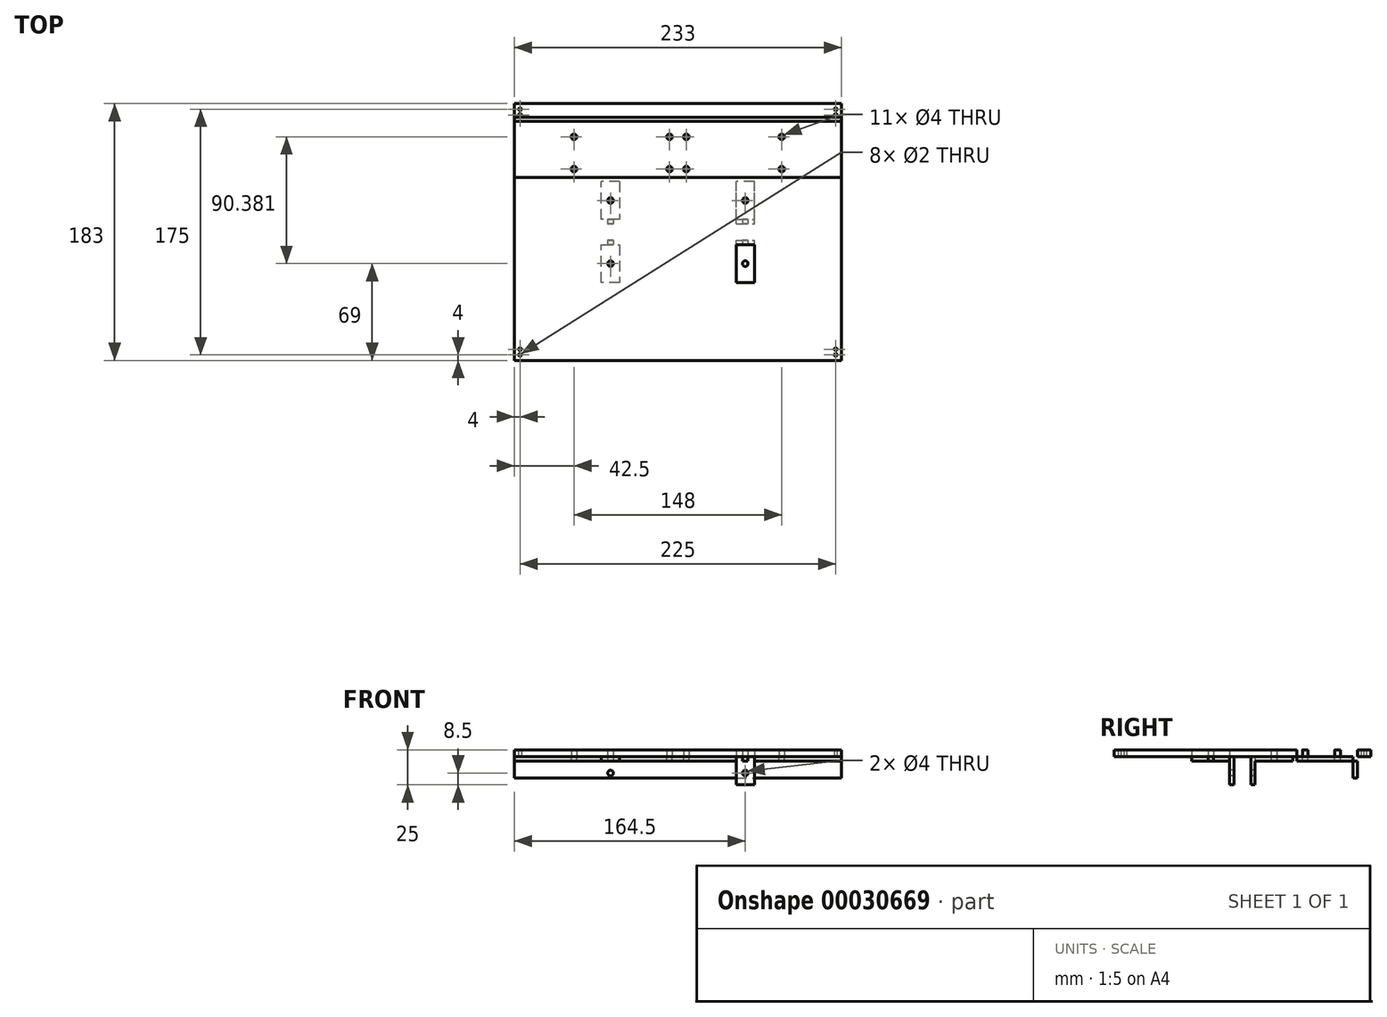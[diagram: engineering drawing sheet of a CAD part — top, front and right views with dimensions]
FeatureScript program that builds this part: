
annotation { "Feature Type Name" : "Feature", "Feature Type Description" : "" }
export const myFeature = defineFeature(function(context is Context, id is Id, definition is map)
    precondition{}
    {
        {
            var Q0;
            Q0=qCreatedBy(makeId("Top.planeOp"),FACE);
            var sketch = newSketch(context, id + "F0", { "sketchPlane" : qUnion([Q0])});
            skLineSegment(sketch, "E0.rect.bottom", {"start": v(116.5, 91.5) * mm, "end": v(-116.5, 91.5) * mm});
            skLineSegment(sketch, "E0.rect.top", {"start": v(116.5, -91.5) * mm, "end": v(-116.5, -91.5) * mm});
            skLineSegment(sketch, "E0.rect.left", {"start": v(116.5, 91.5) * mm, "end": v(116.5, -91.5) * mm});
            skLineSegment(sketch, "E0.rect.right", {"start": v(-116.5, 91.5) * mm, "end": v(-116.5, -91.5) * mm});
            skPoint(sketch, "E0.rect.middle", {"position": v(0, 0) * mm});
            skLineSegment(sketch, "E1", {"start": v(-116.5, -6) * mm, "end": v(116.5, -6) * mm});
            skLineSegment(sketch, "E2.MirrorCS", {"start": v(-116.5, 6) * mm, "end": v(116.5, 6) * mm});
            skLineSegment(sketch, "E3", {"start": v(-116.5, 9) * mm, "end": v(116.5, 9) * mm});
            skLineSegment(sketch, "E4", {"start": v(-116.5, -9) * mm, "end": v(116.5, -9) * mm});
            skLineSegment(sketch, "E5.bottom", {"start": v(-116.5, 6) * mm, "end": v(116.5, 6) * mm, "construction": true});
            skLineSegment(sketch, "E5.top", {"start": v(-116.5, 36) * mm, "end": v(116.5, 36) * mm, "construction": true});
            skLineSegment(sketch, "E5.left", {"start": v(-116.5, 6) * mm, "end": v(-116.5, 36) * mm});
            skLineSegment(sketch, "E5.right", {"start": v(116.5, 6) * mm, "end": v(116.5, 36) * mm});
            skLineSegment(sketch, "E6.bottom", {"start": v(-116.5, -6) * mm, "end": v(116.5, -6) * mm, "construction": true});
            skLineSegment(sketch, "E6.top", {"start": v(-116.5, -36) * mm, "end": v(116.5, -36) * mm, "construction": true});
            skLineSegment(sketch, "E6.left", {"start": v(-116.5, -6) * mm, "end": v(-116.5, -36) * mm});
            skLineSegment(sketch, "E6.right", {"start": v(116.5, -6) * mm, "end": v(116.5, -36) * mm});
            skCircle(sketch, "E7", {"center": v(-112.5, -87.5) * mm, "radius": 1 * mm});
            skCircle(sketch, "E8", {"center": v(-112.5, -83.5) * mm, "radius": 1 * mm});
            skLineSegment(sketch, "E9", {"start": v(-116.5, 0) * mm, "end": v(116.5, 0) * mm, "construction": true});
            skLineSegment(sketch, "E10", {"start": v(0, -91.5) * mm, "end": v(0, 91.5) * mm, "construction": true});
            skCircle(sketch, "E11.MirrorC", {"center": v(-112.5, 83.5) * mm, "radius": 1 * mm});
            skCircle(sketch, "E12.MirrorC", {"center": v(-112.5, 87.5) * mm, "radius": 1 * mm});
            skCircle(sketch, "E13.MirrorC", {"center": v(112.5, -87.5) * mm, "radius": 1 * mm});
            skCircle(sketch, "E14.MirrorC", {"center": v(112.5, -83.5) * mm, "radius": 1 * mm});
            skCircle(sketch, "E15.MirrorC", {"center": v(112.5, 83.5) * mm, "radius": 1 * mm});
            skCircle(sketch, "E16.MirrorC", {"center": v(112.5, 87.5) * mm, "radius": 1 * mm});
            skLineSegment(sketch, "E17", {"start": v(-54.5, -36) * mm, "end": v(-54.5, 36) * mm});
            skLineSegment(sketch, "E18", {"start": v(-41.5, 36) * mm, "end": v(-41.5, -36) * mm});
            skLineSegment(sketch, "E19", {"start": v(54.5, -36) * mm, "end": v(54.5, 36) * mm});
            skLineSegment(sketch, "E20", {"start": v(41.5, -36) * mm, "end": v(41.5, 36) * mm});
            skLineSegment(sketch, "E21", {"start": v(54.5, -36) * mm, "end": v(41.5, -36) * mm});
            skLineSegment(sketch, "E22", {"start": v(-41.5, -36) * mm, "end": v(-54.5, -36) * mm});
            skLineSegment(sketch, "E23", {"start": v(54.5, 36) * mm, "end": v(41.5, 36) * mm});
            skLineSegment(sketch, "E24", {"start": v(-41.5, 36) * mm, "end": v(-54.5, 36) * mm});
            skSolve(sketch);
        }
        {
            var Q0;
            Q0 = qSketchRegion(id + "F0", true);
            var Q1;
            {var subQ1=sQuery(id+"F0.wireOp",EDGE,"E0.rect.bottom");Q1=makeQuery(id+"F0.imprint","IMPRINT",FACE,{"disambiguationData":[TD([[makeQuery(id+"F0.imprint","IMPRINT",EDGE,{"derivedFrom":subQ1}),1.0]])]});}
            var Q2;
            {var subQ5=sQuery(id+"F0.wireOp",EDGE,"E21");Q2=makeQuery(id+"F0.imprint","IMPRINT",FACE,{"disambiguationData":[TD([[makeQuery(id+"F0.imprint","IMPRINT",EDGE,{"derivedFrom":subQ5}),-1.0]])]});}
            var Q3;
            {var subQ5=sQuery(id+"F0.wireOp",EDGE,"E23");Q3=makeQuery(id+"F0.imprint","IMPRINT",FACE,{"disambiguationData":[TD([[makeQuery(id+"F0.imprint","IMPRINT",EDGE,{"derivedFrom":subQ5}),1.0]])]});}
            var Q4;
            {var subQ5=sQuery(id+"F0.wireOp",EDGE,"E24");Q4=makeQuery(id+"F0.imprint","IMPRINT",FACE,{"disambiguationData":[TD([[makeQuery(id+"F0.imprint","IMPRINT",EDGE,{"derivedFrom":subQ5}),1.0]])]});}
            var Q5;
            {var subQ5=sQuery(id+"F0.wireOp",EDGE,"E22");Q5=makeQuery(id+"F0.imprint","IMPRINT",FACE,{"disambiguationData":[TD([[makeQuery(id+"F0.imprint","IMPRINT",EDGE,{"derivedFrom":subQ5}),-1.0]])]});}
            var Q6;
            {var subQ0=sQuery(id+"F0.wireOp",EDGE,"E20");var subQ1=sQuery(id+"F0.wireOp",EDGE,"E1");var subQ2=makeQuery(id+"F0.imprint","INTERSECT",VERTEX,{"derivedFrom":[subQ1,subQ0]});Q6=makeQuery(id+"F0.imprint","IMPRINT",FACE,{"disambiguationData":[TD([[makeQuery(id+"F0.imprint","IMPRINT",EDGE,{"disambiguationData":[TD([[subQ2,-1.0]])],"derivedFrom":subQ1}),1.0]])]});}
            var Q7;
            {var subQ0=sQuery(id+"F0.wireOp",EDGE,"E18");var subQ1=sQuery(id+"F0.wireOp",EDGE,"E1");var subQ2=makeQuery(id+"F0.imprint","INTERSECT",VERTEX,{"derivedFrom":[subQ1,subQ0]});Q7=makeQuery(id+"F0.imprint","IMPRINT",FACE,{"disambiguationData":[TD([[makeQuery(id+"F0.imprint","IMPRINT",EDGE,{"disambiguationData":[TD([[subQ2,-1.0]])],"derivedFrom":subQ1}),1.0]])]});}
            var Q8;
            {var subQ0=sQuery(id+"F0.wireOp",EDGE,"E20");var subQ1=sQuery(id+"F0.wireOp",EDGE,"E2.MirrorCS");var subQ2=makeQuery(id+"F0.imprint","INTERSECT",VERTEX,{"derivedFrom":[subQ1,subQ0]});Q8=makeQuery(id+"F0.imprint","IMPRINT",FACE,{"disambiguationData":[TD([[makeQuery(id+"F0.imprint","IMPRINT",EDGE,{"disambiguationData":[TD([[subQ2,-1.0]])],"derivedFrom":subQ1}),1.0]])]});}
            var Q9;
            {var subQ0=sQuery(id+"F0.wireOp",EDGE,"E20");var subQ1=sQuery(id+"F0.wireOp",EDGE,"E1");var subQ2=makeQuery(id+"F0.imprint","INTERSECT",VERTEX,{"derivedFrom":[subQ1,subQ0]});Q9=makeQuery(id+"F0.imprint","IMPRINT",FACE,{"disambiguationData":[TD([[makeQuery(id+"F0.imprint","IMPRINT",EDGE,{"disambiguationData":[TD([[subQ2,-1.0]])],"derivedFrom":subQ1}),-1.0]])]});}
            var Q10;
            {var subQ0=sQuery(id+"F0.wireOp",EDGE,"E18");var subQ1=sQuery(id+"F0.wireOp",EDGE,"E1");var subQ2=makeQuery(id+"F0.imprint","INTERSECT",VERTEX,{"derivedFrom":[subQ1,subQ0]});Q10=makeQuery(id+"F0.imprint","IMPRINT",FACE,{"disambiguationData":[TD([[makeQuery(id+"F0.imprint","IMPRINT",EDGE,{"disambiguationData":[TD([[subQ2,-1.0]])],"derivedFrom":subQ1}),-1.0]])]});}
            var Q11;
            {var subQ0=sQuery(id+"F0.wireOp",EDGE,"E18");var subQ1=sQuery(id+"F0.wireOp",EDGE,"E2.MirrorCS");var subQ2=makeQuery(id+"F0.imprint","INTERSECT",VERTEX,{"derivedFrom":[subQ1,subQ0]});Q11=makeQuery(id+"F0.imprint","IMPRINT",FACE,{"disambiguationData":[TD([[makeQuery(id+"F0.imprint","IMPRINT",EDGE,{"disambiguationData":[TD([[subQ2,-1.0]])],"derivedFrom":subQ1}),1.0]])]});}
            var Q12;
            {var subQ0=sQuery(id+"F0.wireOp",EDGE,"E17");var subQ1=sQuery(id+"F0.wireOp",EDGE,"E1");var subQ2=makeQuery(id+"F0.imprint","INTERSECT",VERTEX,{"derivedFrom":[subQ1,subQ0]});Q12=makeQuery(id+"F0.imprint","IMPRINT",FACE,{"disambiguationData":[TD([[makeQuery(id+"F0.imprint","IMPRINT",EDGE,{"disambiguationData":[TD([[subQ2,-1.0]])],"derivedFrom":subQ1}),1.0]])]});}
            var Q13;
            {var subQ0=sQuery(id+"F0.wireOp",EDGE,"E17");var subQ1=sQuery(id+"F0.wireOp",EDGE,"E2.MirrorCS");var subQ2=makeQuery(id+"F0.imprint","INTERSECT",VERTEX,{"derivedFrom":[subQ1,subQ0]});Q13=makeQuery(id+"F0.imprint","IMPRINT",FACE,{"disambiguationData":[TD([[makeQuery(id+"F0.imprint","IMPRINT",EDGE,{"disambiguationData":[TD([[subQ2,-1.0]])],"derivedFrom":subQ1}),1.0]])]});}
            var Q14;
            {var subQ0=sQuery(id+"F0.wireOp",EDGE,"E17");var subQ1=sQuery(id+"F0.wireOp",EDGE,"E1");var subQ2=makeQuery(id+"F0.imprint","INTERSECT",VERTEX,{"derivedFrom":[subQ1,subQ0]});Q14=makeQuery(id+"F0.imprint","IMPRINT",FACE,{"disambiguationData":[TD([[makeQuery(id+"F0.imprint","IMPRINT",EDGE,{"disambiguationData":[TD([[subQ2,-1.0]])],"derivedFrom":subQ1}),-1.0]])]});}
            extrude(context, id + "F1", {"entities" : qUnion([Q0, Q1, Q2, Q3, Q4, Q5, Q6, Q7, Q8, Q9, Q10, Q11, Q12, Q13, Q14]), "depth" : 5 * mm});
        }
        {
            var Q0;
            {var subQ0=sQuery(id+"F0.wireOp",EDGE,"E17");var subQ1=sQuery(id+"F0.wireOp",EDGE,"E1");var subQ2=makeQuery(id+"F0.imprint","INTERSECT",VERTEX,{"derivedFrom":[subQ1,subQ0]});Q0=makeQuery(id+"F0.imprint","IMPRINT",FACE,{"disambiguationData":[TD([[makeQuery(id+"F0.imprint","IMPRINT",EDGE,{"disambiguationData":[TD([[subQ2,-1.0]])],"derivedFrom":subQ1}),-1.0]])]});}
            var Q1;
            {var subQ0=sQuery(id+"F0.wireOp",EDGE,"E20");var subQ1=sQuery(id+"F0.wireOp",EDGE,"E1");var subQ2=makeQuery(id+"F0.imprint","INTERSECT",VERTEX,{"derivedFrom":[subQ1,subQ0]});Q1=makeQuery(id+"F0.imprint","IMPRINT",FACE,{"disambiguationData":[TD([[makeQuery(id+"F0.imprint","IMPRINT",EDGE,{"disambiguationData":[TD([[subQ2,-1.0]])],"derivedFrom":subQ1}),-1.0]])]});}
            var Q2;
            {var subQ0=sQuery(id+"F0.wireOp",EDGE,"E17");var subQ1=sQuery(id+"F0.wireOp",EDGE,"E2.MirrorCS");var subQ2=makeQuery(id+"F0.imprint","INTERSECT",VERTEX,{"derivedFrom":[subQ1,subQ0]});Q2=makeQuery(id+"F0.imprint","IMPRINT",FACE,{"disambiguationData":[TD([[makeQuery(id+"F0.imprint","IMPRINT",EDGE,{"disambiguationData":[TD([[subQ2,-1.0]])],"derivedFrom":subQ1}),1.0]])]});}
            var Q3;
            {var subQ0=sQuery(id+"F0.wireOp",EDGE,"E20");var subQ1=sQuery(id+"F0.wireOp",EDGE,"E2.MirrorCS");var subQ2=makeQuery(id+"F0.imprint","INTERSECT",VERTEX,{"derivedFrom":[subQ1,subQ0]});Q3=makeQuery(id+"F0.imprint","IMPRINT",FACE,{"disambiguationData":[TD([[makeQuery(id+"F0.imprint","IMPRINT",EDGE,{"disambiguationData":[TD([[subQ2,-1.0]])],"derivedFrom":subQ1}),1.0]])]});}
            extrude(context, id + "F2", {"entities" : qUnion([Q0, Q1, Q2, Q3]), "oppositeDirection" : true, "depth" : 20 * mm});
        }
        {
            var Q0;
            Q0=makeQuery(id+"F2.opExtrude","SWEPT_FACE",FACE,{"disambiguationData":[OSD([sQuery(id+"F0.wireOp",EDGE,"E4")])]});
            var sketch = newSketch(context, id + "F3", { "sketchPlane" : qUnion([Q0])});
            skLineSegment(sketch, "E25.bottom", {"start": v(-54.5, 0) * mm, "end": v(-54.5, 0) * mm});
            skLineSegment(sketch, "E25.top", {"start": v(-54.5, -3) * mm, "end": v(-54.5, -3) * mm});
            skLineSegment(sketch, "E25.left", {"start": v(-54.5, 0) * mm, "end": v(-54.5, -3) * mm});
            skLineSegment(sketch, "E25.right", {"start": v(-54.5, 0) * mm, "end": v(-54.5, -3) * mm});
            skLineSegment(sketch, "E26", {"start": v(46, -3) * mm, "end": v(46, -20) * mm, "construction": true});
            skLineSegment(sketch, "E27", {"start": v(50, -3) * mm, "end": v(50, -20) * mm, "construction": true});
            skPoint(sketch, "E28", {"position": v(46, -11.5) * mm});
            skLineSegment(sketch, "E29", {"start": v(46, -11.5) * mm, "end": v(50, -11.5) * mm, "construction": true});
            skCircle(sketch, "E30", {"center": v(48, -11.5) * mm, "radius": 2 * mm});
            skLineSegment(sketch, "E31", {"start": v(-48, -3) * mm, "end": v(-48, -20) * mm, "construction": true});
            skCircle(sketch, "E32.MirrorC", {"center": v(-144, -11.5) * mm, "radius": 2 * mm});
            skLineSegment(sketch, "E33.0", {"start": v(-54.5, -20) * mm, "end": v(-54.5, -20) * mm});
            skPoint(sketch, "E34.0", {"position": v(0, 0) * mm});
            skLineSegment(sketch, "E35", {"start": v(0, 0) * mm, "end": v(0, -27.38) * mm, "construction": true});
            skCircle(sketch, "E36.MirrorC", {"center": v(-48, -11.5) * mm, "radius": 2 * mm});
            skSolve(sketch);
        }
        {
            var Q0;
            {var subQ5=sQuery(id+"F0.wireOp",EDGE,"E21");Q0=makeQuery(id+"F0.imprint","IMPRINT",FACE,{"disambiguationData":[TD([[makeQuery(id+"F0.imprint","IMPRINT",EDGE,{"derivedFrom":subQ5}),-1.0]])]});}
            var Q1;
            {var subQ5=sQuery(id+"F0.wireOp",EDGE,"E22");Q1=makeQuery(id+"F0.imprint","IMPRINT",FACE,{"disambiguationData":[TD([[makeQuery(id+"F0.imprint","IMPRINT",EDGE,{"derivedFrom":subQ5}),-1.0]])]});}
            var Q2;
            {var subQ5=sQuery(id+"F0.wireOp",EDGE,"E23");Q2=makeQuery(id+"F0.imprint","IMPRINT",FACE,{"disambiguationData":[TD([[makeQuery(id+"F0.imprint","IMPRINT",EDGE,{"derivedFrom":subQ5}),1.0]])]});}
            var Q3;
            {var subQ5=sQuery(id+"F0.wireOp",EDGE,"E24");Q3=makeQuery(id+"F0.imprint","IMPRINT",FACE,{"disambiguationData":[TD([[makeQuery(id+"F0.imprint","IMPRINT",EDGE,{"derivedFrom":subQ5}),1.0]])]});}
            extrude(context, id + "F4", {"entities" : qUnion([Q0, Q1, Q2, Q3]), "operationType" : NewBodyOperationType.ADD, "oppositeDirection" : true, "depth" : 3 * mm});
        }
        {
            var Q0;
            Q0=makeQuery(id+"F3.imprint","IMPRINT",FACE,{"disambiguationData":[TD([[makeQuery(id+"F3.imprint","IMPRINT",EDGE,{"derivedFrom":sQuery(id+"F3.wireOp",EDGE,"E30")}),1.0]])]});
            var Q1;
            Q1=makeQuery(id+"F3.imprint","IMPRINT",FACE,{"disambiguationData":[TD([[makeQuery(id+"F3.imprint","IMPRINT",EDGE,{"derivedFrom":sQuery(id+"F3.wireOp",EDGE,"E36.MirrorC")}),-1.0]])]});
            var Q2;
            Q2=makeQuery(id+"F2.opExtrude","SWEPT_FACE",FACE,{"disambiguationData":[OSD([sQuery(id+"F0.wireOp",EDGE,"E3")])]});
            extrude(context, id + "F5", {"entities" : qUnion([Q0, Q1]), "operationType" : NewBodyOperationType.REMOVE, "endBound" : BoundingType.UP_TO_SURFACE, "oppositeDirection" : true, "endBoundEntityFace" : qUnion([Q2]), "depth" : 25 * mm});
        }
        {
            var Q0;
            Q0=makeQuery(id+"F4.opExtrude","CAP_FACE",FACE,{"disambiguationData":[OSD([sQuery(id+"F0.wireOp",EDGE,"E4"),sQuery(id+"F0.wireOp",EDGE,"E19"),sQuery(id+"F0.wireOp",EDGE,"E20"),sQuery(id+"F0.wireOp",EDGE,"E21")])],"isStart":false});
            var sketch = newSketch(context, id + "F6", { "sketchPlane" : qUnion([Q0])});
            skLineSegment(sketch, "E37", {"start": v(-50, 36) * mm, "end": v(-50, 9) * mm, "construction": true});
            skLineSegment(sketch, "E38", {"start": v(-46, 36) * mm, "end": v(-46, 9) * mm, "construction": true});
            skLineSegment(sketch, "E39", {"start": v(-50, 22.5) * mm, "end": v(-46, 22.5) * mm, "construction": true});
            skCircle(sketch, "E40", {"center": v(-48, 22.5) * mm, "radius": 2 * mm});
            skCircle(sketch, "E41.MirrorC", {"center": v(48, 22.5) * mm, "radius": 2 * mm});
            skLineSegment(sketch, "E42.0.0", {"start": v(-54.5, 9) * mm, "end": v(-41.5, 9) * mm});
            skLineSegment(sketch, "E42.0.1", {"start": v(-41.5, 9) * mm, "end": v(-41.5, 36) * mm});
            skLineSegment(sketch, "E42.0.2", {"start": v(-41.5, 36) * mm, "end": v(-54.5, 36) * mm});
            skLineSegment(sketch, "E42.0.3", {"start": v(-54.5, 36) * mm, "end": v(-54.5, 9) * mm});
            skLineSegment(sketch, "E42.2", {"start": v(-41.5, 36) * mm, "end": v(-54.5, 36) * mm});
            skSolve(sketch);
        }
        {
            var Q0;
            Q0=makeQuery(id+"F6.imprint","IMPRINT",FACE,{"disambiguationData":[TD([[makeQuery(id+"F6.imprint","IMPRINT",EDGE,{"derivedFrom":sQuery(id+"F6.wireOp",EDGE,"E41.MirrorC")}),-1.0]])]});
            var Q1;
            Q1=makeQuery(id+"F6.imprint","IMPRINT",FACE,{"disambiguationData":[TD([[makeQuery(id+"F6.imprint","IMPRINT",EDGE,{"derivedFrom":sQuery(id+"F6.wireOp",EDGE,"E40")}),1.0]])]});
            extrude(context, id + "F7", {"entities" : qUnion([Q0, Q1]), "operationType" : NewBodyOperationType.REMOVE, "oppositeDirection" : true, "depth" : 25 * mm});
        }
        {
            var Q0;
            Q0=makeQuery(id+"F4.opExtrude","CAP_FACE",FACE,{"disambiguationData":[OSD([sQuery(id+"F0.wireOp",EDGE,"E3"),sQuery(id+"F0.wireOp",EDGE,"E19"),sQuery(id+"F0.wireOp",EDGE,"E20"),sQuery(id+"F0.wireOp",EDGE,"E23")])],"isStart":false});
            var sketch = newSketch(context, id + "F8", { "sketchPlane" : qUnion([Q0])});
            skLineSegment(sketch, "E43", {"start": v(-50, -9) * mm, "end": v(-50, -36) * mm, "construction": true});
            skLineSegment(sketch, "E44", {"start": v(-46, -9) * mm, "end": v(-46, -36) * mm, "construction": true});
            skLineSegment(sketch, "E45", {"start": v(-50, -22.5) * mm, "end": v(-46, -22.5) * mm, "construction": true});
            skCircle(sketch, "E46", {"center": v(-48, -22.5) * mm, "radius": 2 * mm});
            skLineSegment(sketch, "E47", {"start": v(0, 0) * mm, "end": v(0, -91.5) * mm, "construction": true});
            skCircle(sketch, "E48.MirrorC", {"center": v(48, -22.5) * mm, "radius": 2 * mm});
            skSolve(sketch);
        }
        {
            var Q0;
            Q0 = qSketchRegion(id + "F8", true);
            extrude(context, id + "F9", {"entities" : qUnion([Q0]), "operationType" : NewBodyOperationType.REMOVE, "oppositeDirection" : true, "depth" : 25 * mm});
        }
        {
            var Q0;
            Q0=qCreatedBy(makeId("Top.planeOp"),FACE);
            var sketch = newSketch(context, id + "F10", { "sketchPlane" : qUnion([Q0])});
            skLineSegment(sketch, "E49.bottom", {"start": v(-116.5, 38.88) * mm, "end": v(116.5, 38.88) * mm});
            skLineSegment(sketch, "E49.top", {"start": v(-116.5, 81.88) * mm, "end": v(116.5, 81.88) * mm});
            skLineSegment(sketch, "E49.left", {"start": v(-116.5, 38.88) * mm, "end": v(-116.5, 81.88) * mm});
            skLineSegment(sketch, "E49.right", {"start": v(116.5, 38.88) * mm, "end": v(116.5, 81.88) * mm});
            skLineSegment(sketch, "E50.bottom", {"start": v(0, 38.88) * mm, "end": v(-80, 38.88) * mm, "construction": true});
            skLineSegment(sketch, "E50.top", {"start": v(0, 73.88) * mm, "end": v(-80, 73.88) * mm, "construction": true});
            skLineSegment(sketch, "E50.left", {"start": v(0, 38.88) * mm, "end": v(0, 73.88) * mm, "construction": true});
            skLineSegment(sketch, "E50.right", {"start": v(-80, 38.88) * mm, "end": v(-80, 73.88) * mm, "construction": true});
            skLineSegment(sketch, "E51.bottom", {"start": v(0, 38.88) * mm, "end": v(80, 38.88) * mm, "construction": true});
            skCircle(sketch, "E52", {"center": v(-6, 44.88) * mm, "radius": 2 * mm});
            skLineSegment(sketch, "E53", {"start": v(-80, 56.38) * mm, "end": v(0, 56.38) * mm, "construction": true});
            skLineSegment(sketch, "E54", {"start": v(-40, 38.88) * mm, "end": v(-40, 73.88) * mm, "construction": true});
            skCircle(sketch, "E55.MirrorC", {"center": v(-74, 44.88) * mm, "radius": 2 * mm});
            skCircle(sketch, "E56.MirrorC", {"center": v(-74, 67.88) * mm, "radius": 2 * mm});
            skCircle(sketch, "E57.MirrorC", {"center": v(-6, 67.88) * mm, "radius": 2 * mm});
            skCircle(sketch, "E58.MirrorC", {"center": v(6, 44.88) * mm, "radius": 2 * mm});
            skCircle(sketch, "E59.MirrorC", {"center": v(6, 67.88) * mm, "radius": 2 * mm});
            skLineSegment(sketch, "E60.MirrorCS", {"start": v(0, 73.88) * mm, "end": v(80, 73.88) * mm, "construction": true});
            skLineSegment(sketch, "E61.MirrorCS", {"start": v(80, 38.88) * mm, "end": v(80, 73.88) * mm, "construction": true});
            skCircle(sketch, "E62.MirrorC", {"center": v(74, 44.88) * mm, "radius": 2 * mm});
            skCircle(sketch, "E63.MirrorC", {"center": v(74, 67.88) * mm, "radius": 2 * mm});
            skSolve(sketch);
        }
        {
            var Q0;
            Q0 = qSketchRegion(id + "F10", true);
            extrude(context, id + "F11", {"entities" : qUnion([Q0]), "oppositeDirection" : true, "depth" : 3 * mm});
        }
        {
            var Q0;
            Q0=makeQuery(id+"F11.opExtrude","CAP_FACE",FACE,{"disambiguationData":[OSD([sQuery(id+"F10.wireOp",EDGE,"E49.bottom"),sQuery(id+"F10.wireOp",EDGE,"E49.top"),sQuery(id+"F10.wireOp",EDGE,"E49.left"),sQuery(id+"F10.wireOp",EDGE,"E49.right")])],"isStart":true});
            var sketch = newSketch(context, id + "F12", { "sketchPlane" : qUnion([Q0])});
            skLineSegment(sketch, "E64.bottom", {"start": v(-116.5, 81.88) * mm, "end": v(-113.2, 81.88) * mm});
            skLineSegment(sketch, "E64.top", {"start": v(-116.5, 38.88) * mm, "end": v(-113.2, 38.88) * mm});
            skLineSegment(sketch, "E64.left", {"start": v(-116.5, 81.88) * mm, "end": v(-116.5, 38.88) * mm});
            skLineSegment(sketch, "E64.right", {"start": v(-113.2, 81.88) * mm, "end": v(-113.2, 38.88) * mm});
            skLineSegment(sketch, "E65.bottom", {"start": v(116.5, 81.88) * mm, "end": v(113.2, 81.88) * mm});
            skLineSegment(sketch, "E65.top", {"start": v(116.5, 38.88) * mm, "end": v(113.2, 38.88) * mm});
            skLineSegment(sketch, "E65.left", {"start": v(116.5, 81.88) * mm, "end": v(116.5, 38.88) * mm});
            skLineSegment(sketch, "E65.right", {"start": v(113.2, 81.88) * mm, "end": v(113.2, 38.88) * mm});
            skSolve(sketch);
        }
        {
            var Q0;
            Q0 = qSketchRegion(id + "F10", true);
            extrude(context, id + "F13", {"entities" : qUnion([Q0]), "operationType" : NewBodyOperationType.REMOVE, "depth" : 25 * mm});
        }
        {
            var Q0;
            Q0=makeQuery(id+"F11.opExtrude","CAP_FACE",FACE,{"disambiguationData":[OSD([sQuery(id+"F10.wireOp",EDGE,"E49.bottom"),sQuery(id+"F10.wireOp",EDGE,"E49.top"),sQuery(id+"F10.wireOp",EDGE,"E49.left"),sQuery(id+"F10.wireOp",EDGE,"E49.right"),sQuery(id+"F10.wireOp",EDGE,"E52"),sQuery(id+"F10.wireOp",EDGE,"E55.MirrorC"),sQuery(id+"F10.wireOp",EDGE,"E56.MirrorC"),sQuery(id+"F10.wireOp",EDGE,"E57.MirrorC"),sQuery(id+"F10.wireOp",EDGE,"6fd4ff58-d2f7-42ed-b95d-34c13335608c0.MirrorC"),sQuery(id+"F10.wireOp",EDGE,"1a3a4e10-e711-496e-9766-84adcd70d5de0.MirrorC"),sQuery(id+"F10.wireOp",EDGE,"2bd374fb-c7d1-456d-8e91-df995c6d3f900.MirrorC"),sQuery(id+"F10.wireOp",EDGE,"aede4349-2fd3-4573-86dd-ba3ae19f021d0.MirrorC")])],"isStart":false});
            var sketch = newSketch(context, id + "F14", { "sketchPlane" : qUnion([Q0])});
            skLineSegment(sketch, "E66.bottom", {"start": v(-116.5, -78.88) * mm, "end": v(116.5, -78.88) * mm});
            skLineSegment(sketch, "E66.top", {"start": v(-116.5, -81.88) * mm, "end": v(116.5, -81.88) * mm});
            skLineSegment(sketch, "E66.left", {"start": v(-116.5, -78.88) * mm, "end": v(-116.5, -81.88) * mm});
            skLineSegment(sketch, "E66.right", {"start": v(116.5, -78.88) * mm, "end": v(116.5, -81.88) * mm});
            skSolve(sketch);
        }
        {
            var Q0;
            Q0 = qSketchRegion(id + "F14", true);
            extrude(context, id + "F15", {"entities" : qUnion([Q0]), "operationType" : NewBodyOperationType.ADD, "depth" : 12 * mm});
        }
        {
            var Q0;
            Q0 = qSketchRegion(id + "F14", true);
            var Q1;
            Q1 = qSketchRegion(id + "F12", true);
            var Q2;
            Q2 = qSketchRegion(id + "F10", true);
            extrude(context, id + "F16", {"entities" : qUnion([Q0, Q1, Q2]), "operationType" : NewBodyOperationType.REMOVE, "oppositeDirection" : true, "depth" : 25 * mm});
        }
    });
